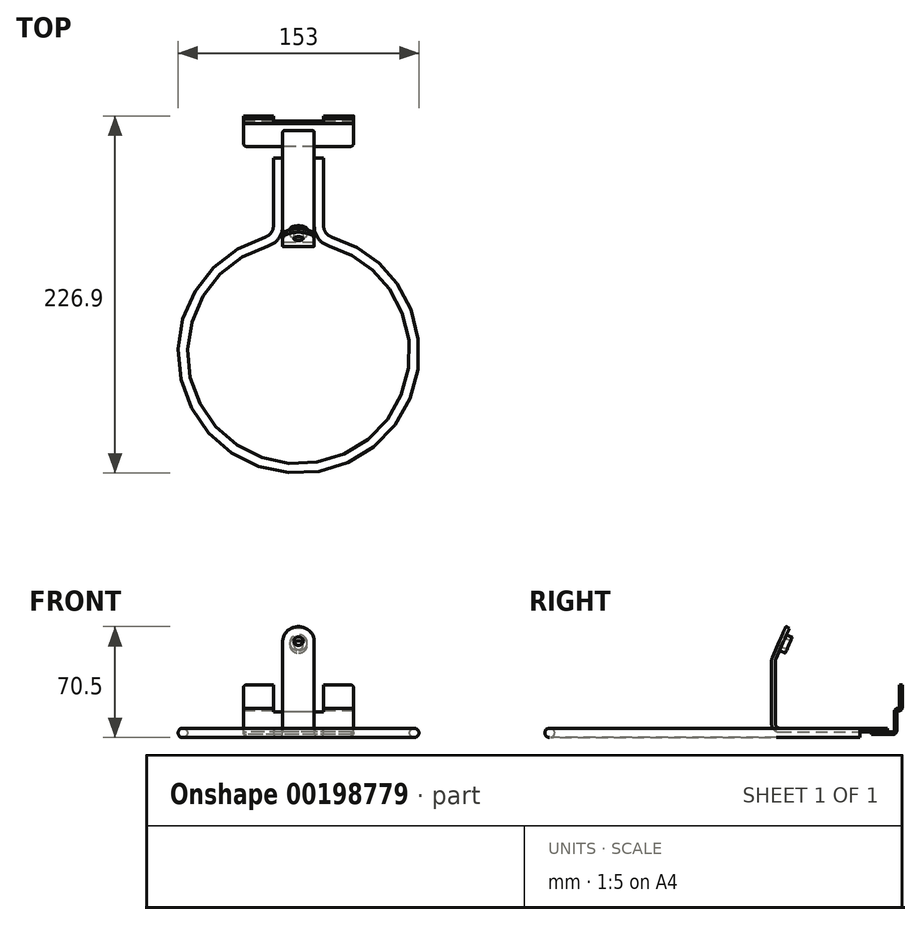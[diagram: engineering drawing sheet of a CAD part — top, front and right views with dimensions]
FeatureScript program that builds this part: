
annotation { "Feature Type Name" : "Feature", "Feature Type Description" : "" }
export const myFeature = defineFeature(function(context is Context, id is Id, definition is map)
    precondition{}
    {
        {
            var Q0;
            Q0=qCreatedBy(makeId("Top.planeOp"),FACE);
            var sketch = newSketch(context, id + "F0", { "sketchPlane" : qUnion([Q0])});
            skArc(sketch, "E0", {"start": v(-20.25, 70.66) * mm, "mid": v(0, -73.5) * mm, "end": v(20.25, 70.66) * mm});
            skLineSegment(sketch, "E1", {"start": v(0, -73.5) * mm, "end": v(0, 123.5) * mm, "construction": true});
            skLineSegment(sketch, "E2.0", {"start": v(13, 80.27) * mm, "end": v(13, 123.5) * mm});
            skLineSegment(sketch, "E3", {"start": v(0, 123.5) * mm, "end": v(13, 123.5) * mm, "construction": true});
            skLineSegment(sketch, "E4.MirrorCS", {"start": v(-13, 80.27) * mm, "end": v(-13, 123.5) * mm});
            skPoint(sketch, "E5.visualSharp", {"position": v(13, 72.34) * mm});
            skArc(sketch, "E5.filletArc", {"start": v(13, 80.27) * mm, "mid": v(15.01, 74.25) * mm, "end": v(20.25, 70.66) * mm});
            skPoint(sketch, "E6.visualSharp", {"position": v(-13, 72.34) * mm});
            skArc(sketch, "E6.filletArc", {"start": v(-20.25, 70.66) * mm, "mid": v(-15.01, 74.25) * mm, "end": v(-13, 80.27) * mm});
            skSolve(sketch);
        }
        {
            var Q0;
            Q0=qCreatedBy(makeId("Front.planeOp"),FACE);
            var Q1;
            Q1=sQuery(id+"F0.wireOp",VERTEX,"E3.start");
            cPlane(context, id + "F1", {"entities" : qUnion([Q0, Q1]), "cplaneType" : CPlaneType.PLANE_POINT, "offset" : 25 * mm, "width" : 150 * mm, "height" : 150 * mm});
        }
        {
            var Q0;
            Q0=qCreatedBy(id+"F1.planeOp",FACE);
            var sketch = newSketch(context, id + "F2", { "sketchPlane" : qUnion([Q0])});
            skCircle(sketch, "E7", {"center": v(13, 0) * mm, "radius": 3 * mm});
            skSolve(sketch);
        }
        {
            var Q0;
            Q0=makeQuery(id+"F2.imprint","IMPRINT",FACE,{"disambiguationData":[TD([[makeQuery(id+"F2.imprint","IMPRINT",EDGE,{"derivedFrom":sQuery(id+"F2.wireOp",EDGE,"E7")}),1.0]])]});
            var Q1;
            Q1=sQuery(id+"F0.wireOp",EDGE,"E2.0");
            var Q2;
            Q2=sQuery(id+"F0.wireOp",EDGE,"E5.filletArc");
            var Q3;
            Q3=sQuery(id+"F0.wireOp",EDGE,"E0");
            var Q4;
            Q4=sQuery(id+"F0.wireOp",EDGE,"E6.filletArc");
            var Q5;
            Q5=sQuery(id+"F0.wireOp",EDGE,"E4.MirrorCS");
            sweep(context, id + "F3", {"profiles" : qUnion([Q0]), "path" : qUnion([Q1, Q2, Q3, Q4, Q5])});
        }
        {
            var Q0;
            Q0=qCreatedBy(makeId("Right.planeOp"),FACE);
            var sketch = newSketch(context, id + "F4", { "sketchPlane" : qUnion([Q0])});
            skLineSegment(sketch, "E8", {"start": v(72.5, 3) * mm, "end": v(141, 3) * mm});
            skLineSegment(sketch, "E9", {"start": v(70, 5.5) * mm, "end": v(70, 45.97) * mm});
            skLineSegment(sketch, "E10", {"start": v(70.21, 46.98) * mm, "end": v(78.79, 66.5) * mm});
            skPoint(sketch, "E11.visualSharp", {"position": v(70, 3) * mm});
            skArc(sketch, "E11.filletArc", {"start": v(70, 5.5) * mm, "mid": v(70.73, 3.73) * mm, "end": v(72.5, 3) * mm});
            skPoint(sketch, "E12.visualSharp", {"position": v(70, 46.5) * mm});
            skArc(sketch, "E12.filletArc", {"start": v(70.21, 46.98) * mm, "mid": v(70.05, 46.49) * mm, "end": v(70, 45.97) * mm});
            skLineSegment(sketch, "E13.0", {"start": v(67.92, 47.99) * mm, "end": v(76.5, 67.5) * mm});
            skLineSegment(sketch, "E13.1", {"start": v(72.5, 0.5) * mm, "end": v(141, 0.5) * mm});
            skArc(sketch, "E13.2", {"start": v(67.5, 5.5) * mm, "mid": v(68.96, 1.96) * mm, "end": v(72.5, 0.5) * mm});
            skLineSegment(sketch, "E13.3", {"start": v(67.5, 5.5) * mm, "end": v(67.5, 45.97) * mm});
            skArc(sketch, "E13.4", {"start": v(67.92, 47.99) * mm, "mid": v(67.6, 47) * mm, "end": v(67.5, 45.97) * mm});
            skLineSegment(sketch, "E14", {"start": v(76.5, 67.5) * mm, "end": v(78.79, 66.5) * mm});
            skLineSegment(sketch, "E15", {"start": v(141, 3) * mm, "end": v(141, 0.5) * mm});
            skSolve(sketch);
        }
        {
            var Q0;
            Q0 = qSketchRegion(id + "F4", true);
            extrude(context, id + "F5", {"entities" : qUnion([Q0]), "depth" : 20 * mm, "symmetric" : true});
        }
        {
            var Q0;
            Q0=makeQuery(id+"F5.opExtrude","CAP_EDGE",EDGE,{"disambiguationData":[OSD([sQuery(id+"F4.wireOp",EDGE,"E14")])],"isStart":false});
            var Q1;
            Q1=makeQuery(id+"F5.opExtrude","CAP_EDGE",EDGE,{"disambiguationData":[OSD([sQuery(id+"F4.wireOp",EDGE,"E14")])],"isStart":true});
            fillet(context, id + "F6", {"entities" : qUnion([Q0, Q1]), "radius" : 10 * mm, "tangentPropagation" : true, "allowEdgeOverflow" : false});
        }
        {
            var Q0;
            Q0=makeQuery(id+"F5.opExtrude","SWEPT_FACE",FACE,{"disambiguationData":[OSD([sQuery(id+"F4.wireOp",EDGE,"E13.0")])]});
            var sketch = newSketch(context, id + "F7", { "sketchPlane" : qUnion([Q0])});
            skCircle(sketch, "E16", {"center": v(0, 82.58) * mm, "radius": 4.5 * mm});
            skSolve(sketch);
        }
        {
            var Q0;
            Q0 = qSketchRegion(id + "F7", true);
            extrude(context, id + "F8", {"entities" : qUnion([Q0]), "operationType" : NewBodyOperationType.REMOVE, "endBound" : BoundingType.THROUGH_ALL, "oppositeDirection" : true, "depth" : 25 * mm});
        }
        {
            var Q0;
            Q0=makeQuery(id+"F5.opExtrude","CAP_EDGE",EDGE,{"disambiguationData":[OSD([sQuery(id+"F4.wireOp",EDGE,"E15")])],"isStart":true});
            var Q1;
            Q1=makeQuery(id+"F5.opExtrude","CAP_EDGE",EDGE,{"disambiguationData":[OSD([sQuery(id+"F4.wireOp",EDGE,"E15")])],"isStart":false});
            fillet(context, id + "F9", {"entities" : qUnion([Q0, Q1]), "radius" : 1 * mm, "tangentPropagation" : true, "allowEdgeOverflow" : false});
        }
        {
            var Q0;
            Q0=qCreatedBy(makeId("Right.planeOp"),FACE);
            var sketch = newSketch(context, id + "F10", { "sketchPlane" : qUnion([Q0])});
            skLineSegment(sketch, "E17.0", {"start": v(131, 0.5) * mm, "end": v(144.4, 0.5) * mm});
            skPoint(sketch, "E18.orphan", {"position": v(140, 0.5) * mm});
            skPoint(sketch, "E19.orphan", {"position": v(72.5, 0.5) * mm});
            skLineSegment(sketch, "E20", {"start": v(145.4, 1.5) * mm, "end": v(145.4, 13.4) * mm});
            skLineSegment(sketch, "E21", {"start": v(147.5, 15.5) * mm, "end": v(148.3, 15.5) * mm});
            skLineSegment(sketch, "E22", {"start": v(148.8, 16) * mm, "end": v(148.8, 30.5) * mm});
            skPoint(sketch, "E23.visualSharp", {"position": v(145.4, 0.5) * mm});
            skArc(sketch, "E23.filletArc", {"start": v(144.4, 0.5) * mm, "mid": v(145.1, 0.8) * mm, "end": v(145.4, 1.5) * mm});
            skPoint(sketch, "E24.visualSharp", {"position": v(145.4, 15.5) * mm});
            skArc(sketch, "E24.filletArc", {"start": v(147.5, 15.5) * mm, "mid": v(146.02, 14.88) * mm, "end": v(145.4, 13.4) * mm});
            skPoint(sketch, "E25.visualSharp", {"position": v(148.8, 15.5) * mm});
            skArc(sketch, "E25.filletArc", {"start": v(148.3, 15.5) * mm, "mid": v(148.65, 15.65) * mm, "end": v(148.8, 16) * mm});
            skLineSegment(sketch, "E26.0", {"start": v(150.4, 16) * mm, "end": v(150.4, 30.5) * mm});
            skLineSegment(sketch, "E26.1", {"start": v(131, -1.1) * mm, "end": v(144.4, -1.1) * mm});
            skArc(sketch, "E26.2", {"start": v(144.4, -1.1) * mm, "mid": v(146.24, -0.34) * mm, "end": v(147, 1.5) * mm});
            skLineSegment(sketch, "E26.3", {"start": v(147, 1.5) * mm, "end": v(147, 13.4) * mm});
            skArc(sketch, "E26.4", {"start": v(148.3, 13.9) * mm, "mid": v(149.78, 14.52) * mm, "end": v(150.4, 16) * mm});
            skLineSegment(sketch, "E27", {"start": v(131, 0.5) * mm, "end": v(131, -1.1) * mm});
            skLineSegment(sketch, "E28", {"start": v(148.8, 30.5) * mm, "end": v(150.4, 30.5) * mm});
            skLineSegment(sketch, "E29", {"start": v(148.3, 13.9) * mm, "end": v(147.5, 13.9) * mm});
            skArc(sketch, "E30.filletArc", {"start": v(147.5, 13.9) * mm, "mid": v(147.15, 13.75) * mm, "end": v(147, 13.4) * mm});
            skSolve(sketch);
        }
        {
            var Q0;
            Q0 = qSketchRegion(id + "F10", true);
            extrude(context, id + "F11", {"entities" : qUnion([Q0]), "operationType" : NewBodyOperationType.ADD, "depth" : 70 * mm, "symmetric" : true});
        }
        {
            var Q0;
            Q0=makeQuery(id+"F11.opExtrude","SWEPT_FACE",FACE,{"disambiguationData":[OSD([sQuery(id+"F10.wireOp",EDGE,"E20")])]});
            var sketch = newSketch(context, id + "F12", { "sketchPlane" : qUnion([Q0])});
            skLineSegment(sketch, "E31", {"start": v(0, 13.4) * mm, "end": v(0, 39.17) * mm, "construction": true});
            skPoint(sketch, "E31.endSnap0", {"position": v(0, 13.4) * mm});
            skLineSegment(sketch, "E32.0", {"start": v(16, 13.4) * mm, "end": v(16, 30.5) * mm});
            skLineSegment(sketch, "E33.0", {"start": v(16, 30.5) * mm, "end": v(-16, 30.5) * mm});
            skLineSegment(sketch, "E34.0", {"start": v(16, 13.4) * mm, "end": v(-16, 13.4) * mm});
            skPoint(sketch, "E35.orphan", {"position": v(35, 30.5) * mm});
            skPoint(sketch, "E36.orphan", {"position": v(35, 13.4) * mm});
            skLineSegment(sketch, "E37.MirrorCS", {"start": v(-16, 13.4) * mm, "end": v(-16, 30.5) * mm});
            skPoint(sketch, "E38.orphan", {"position": v(-35, 30.5) * mm});
            skPoint(sketch, "E39.orphan", {"position": v(-35, 13.4) * mm});
            skSolve(sketch);
        }
        {
            var Q0;
            Q0 = qSketchRegion(id + "F12", true);
            extrude(context, id + "F13", {"entities" : qUnion([Q0]), "operationType" : NewBodyOperationType.REMOVE, "oppositeDirection" : true, "depth" : 25 * mm});
        }
        {
            var Q0;
            Q0=makeQuery(id+"F13.boolean.opBoolean","COPY",EDGE,{"derivedFrom":makeQuery(id+"F13.opExtrude","SWEPT_EDGE",EDGE,{"disambiguationData":[OSD([sQuery(id+"F12.wireOp",EDGE,"E33.0"),sQuery(id+"F12.wireOp",EDGE,"E37.MirrorCS")])]})});
            var Q1;
            Q1=makeQuery(id+"F11.opExtrude","CAP_EDGE",EDGE,{"disambiguationData":[OSD([sQuery(id+"F10.wireOp",EDGE,"E28")])],"isStart":true});
            var Q2;
            Q2=makeQuery(id+"F13.boolean.opBoolean","COPY",EDGE,{"derivedFrom":makeQuery(id+"F13.opExtrude","SWEPT_EDGE",EDGE,{"disambiguationData":[OSD([sQuery(id+"F12.wireOp",EDGE,"E32.0"),sQuery(id+"F12.wireOp",EDGE,"E33.0")])]})});
            var Q3;
            Q3=makeQuery(id+"F11.opExtrude","CAP_EDGE",EDGE,{"disambiguationData":[OSD([sQuery(id+"F10.wireOp",EDGE,"E28")])],"isStart":false});
            var Q4;
            Q4=makeQuery(id+"F11.opExtrude","CAP_EDGE",EDGE,{"disambiguationData":[OSD([sQuery(id+"F10.wireOp",EDGE,"E27")])],"isStart":true});
            var Q5;
            Q5=makeQuery(id+"F11.opExtrude","CAP_EDGE",EDGE,{"disambiguationData":[OSD([sQuery(id+"F10.wireOp",EDGE,"E27")])],"isStart":false});
            fillet(context, id + "F14", {"entities" : qUnion([Q0, Q1, Q2, Q3, Q4, Q5]), "radius" : 2 * mm, "tangentPropagation" : true, "allowEdgeOverflow" : false});
        }
        {
            var Q0;
            Q0=qCreatedBy(makeId("Right.planeOp"),FACE);
            var sketch = newSketch(context, id + "F15", { "sketchPlane" : qUnion([Q0])});
            skLineSegment(sketch, "E40", {"start": v(74.29, 62.46) * mm, "end": v(76.58, 61.46) * mm});
            skLineSegment(sketch, "E41", {"start": v(76.58, 61.46) * mm, "end": v(76.98, 62.37) * mm});
            skLineSegment(sketch, "E42", {"start": v(76.98, 62.37) * mm, "end": v(80.64, 60.76) * mm});
            skLineSegment(sketch, "E43", {"start": v(80.64, 60.76) * mm, "end": v(79.63, 58.48) * mm});
            skLineSegment(sketch, "E44", {"start": v(79.63, 58.48) * mm, "end": v(73.68, 61.1) * mm});
            skLineSegment(sketch, "E45", {"start": v(73.68, 61.1) * mm, "end": v(74.29, 62.46) * mm});
            skLineSegment(sketch, "E46", {"start": v(72.48, 58.35) * mm, "end": v(77.24, 56.25) * mm, "construction": true});
            skSolve(sketch);
        }
        {
            var Q0;
            Q0 = qSketchRegion(id + "F15", true);
            var Q1;
            Q1=sQuery(id+"F15.wireOp",EDGE,"E46");
            revolve(context, id + "F16", {"operationType" : NewBodyOperationType.ADD, "entities" : qUnion([Q0]), "axis" : qUnion([Q1]), "revolveType" : RevolveType.FULL});
        }
    });
